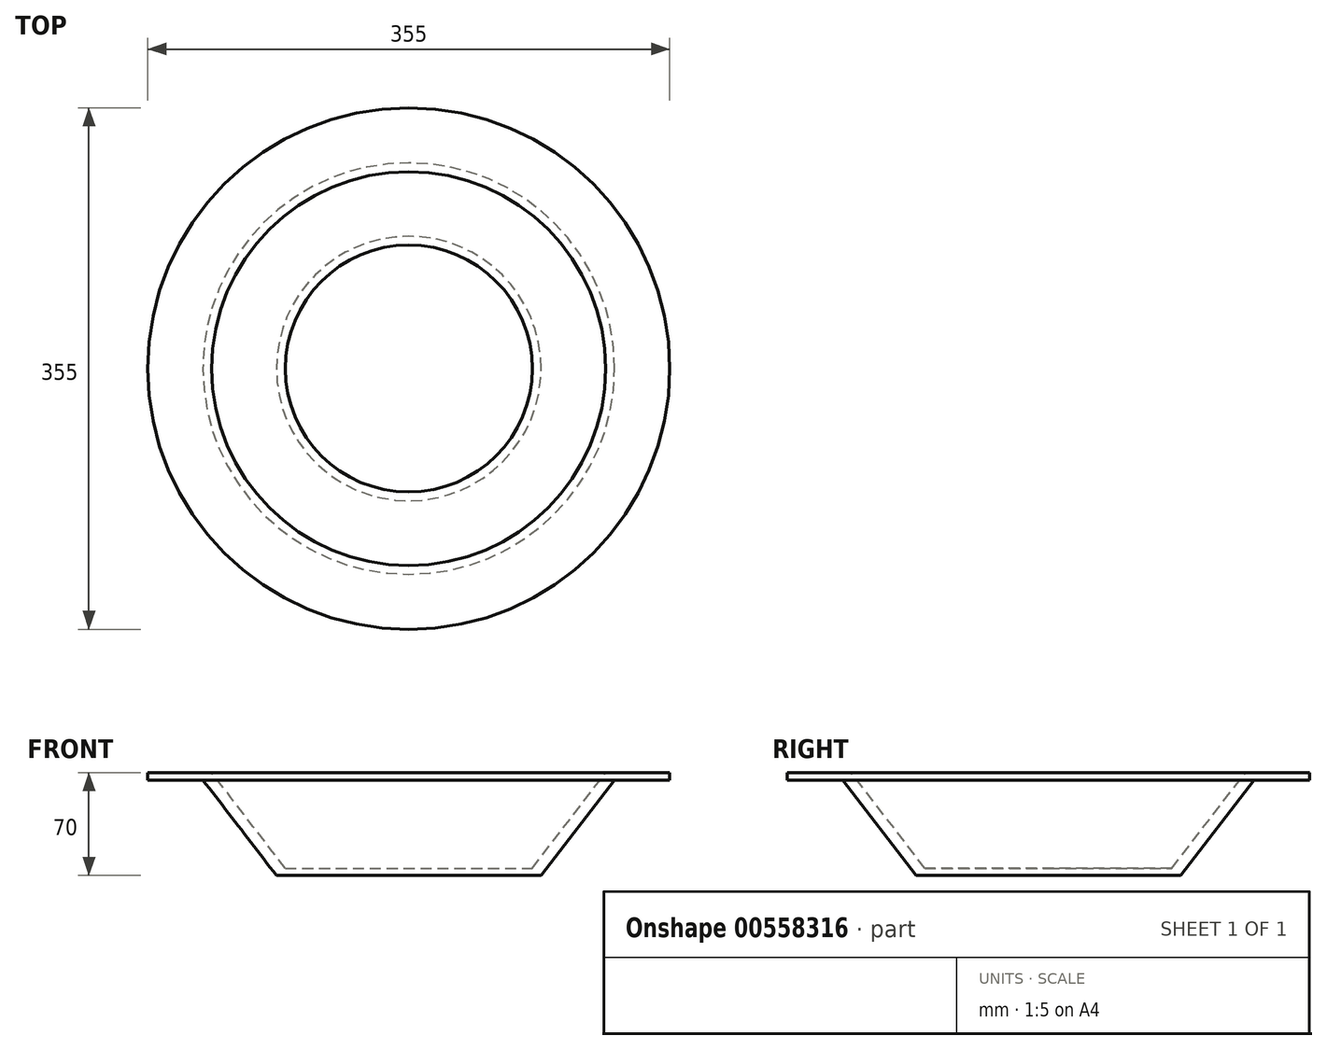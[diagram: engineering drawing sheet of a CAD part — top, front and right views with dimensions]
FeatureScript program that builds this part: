
annotation { "Feature Type Name" : "Feature", "Feature Type Description" : "" }
export const myFeature = defineFeature(function(context is Context, id is Id, definition is map)
    precondition{}
    {
        {
            var Q0;
            Q0=qCreatedBy(makeId("Front.planeOp"),FACE);
            var sketch = newSketch(context, id + "F0", { "sketchPlane" : qUnion([Q0])});
            skLineSegment(sketch, "E0", {"start": v(0, 0) * mm, "end": v(0, 195.45) * mm, "construction": true});
            skLineSegment(sketch, "E1", {"start": v(0, 0) * mm, "end": v(90, 0) * mm});
            skLineSegment(sketch, "E2", {"start": v(90, 0) * mm, "end": v(140, 65) * mm});
            skLineSegment(sketch, "E3", {"start": v(140, 65) * mm, "end": v(177.5, 65) * mm});
            skLineSegment(sketch, "E4", {"start": v(177.5, 65) * mm, "end": v(177.5, 70) * mm});
            skLineSegment(sketch, "E5", {"start": v(177.5, 70) * mm, "end": v(134.02, 70) * mm});
            skLineSegment(sketch, "E6", {"start": v(134.02, 70) * mm, "end": v(84.02, 5) * mm});
            skLineSegment(sketch, "E7", {"start": v(84.02, 5) * mm, "end": v(0, 5) * mm});
            skLineSegment(sketch, "E8", {"start": v(0, 5) * mm, "end": v(0, 0) * mm});
            skSolve(sketch);
        }
        {
            var Q0;
            Q0 = qSketchRegion(id + "F0", true);
            var Q1;
            Q1=sQuery(id+"F0.wireOp",EDGE,"E0");
            revolve(context, id + "F1", {"entities" : qUnion([Q0]), "axis" : qUnion([Q1]), "revolveType" : RevolveType.FULL});
        }
    });
